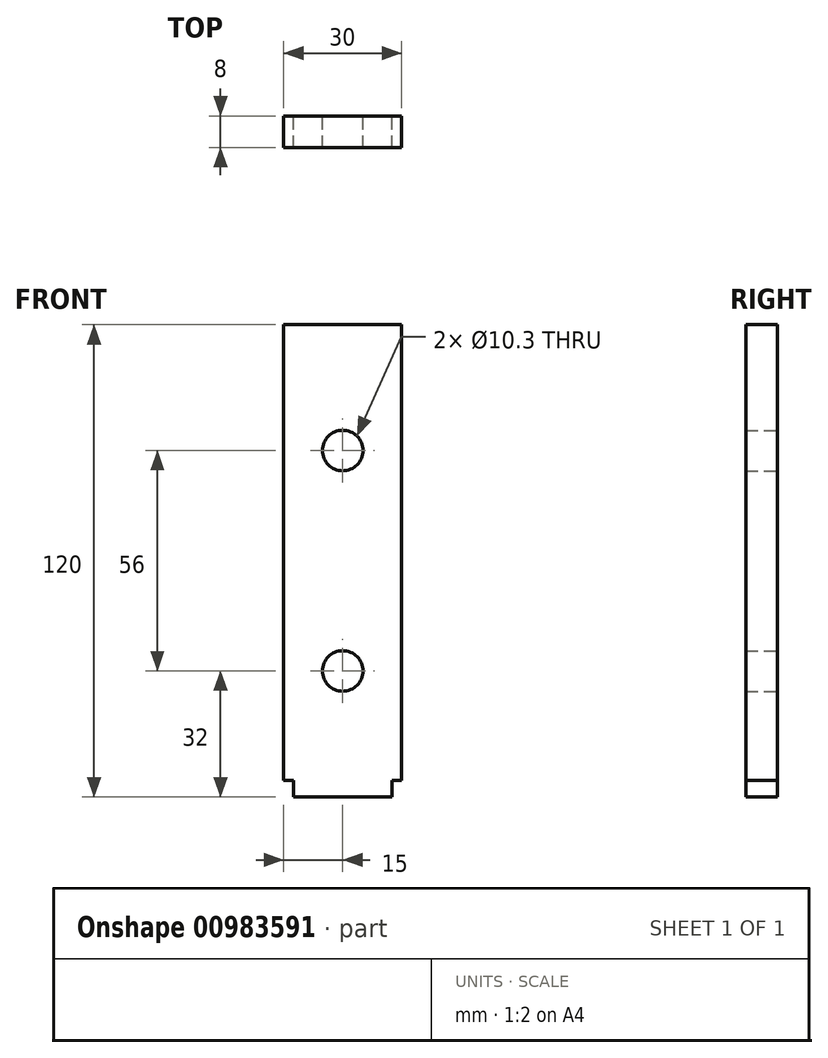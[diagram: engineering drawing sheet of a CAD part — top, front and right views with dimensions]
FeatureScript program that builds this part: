
annotation { "Feature Type Name" : "Feature", "Feature Type Description" : "" }
export const myFeature = defineFeature(function(context is Context, id is Id, definition is map)
    precondition{}
    {
        {
            var Q0;
            Q0=qCreatedBy(makeId("Front.planeOp"),FACE);
            var sketch = newSketch(context, id + "F0", { "sketchPlane" : qUnion([Q0])});
            skLineSegment(sketch, "E0", {"start": v(-15, 0) * mm, "end": v(15, 0) * mm});
            skLineSegment(sketch, "E1", {"start": v(15, 0) * mm, "end": v(15, -115.8) * mm});
            skLineSegment(sketch, "E2", {"start": v(15, -115.8) * mm, "end": v(12.5, -115.8) * mm});
            skLineSegment(sketch, "E3", {"start": v(12.5, -115.8) * mm, "end": v(12.5, -120) * mm});
            skLineSegment(sketch, "E4", {"start": v(12.5, -120) * mm, "end": v(-12.5, -120) * mm});
            skLineSegment(sketch, "E5", {"start": v(-12.5, -120) * mm, "end": v(-12.5, -115.8) * mm});
            skLineSegment(sketch, "E6", {"start": v(-12.5, -115.8) * mm, "end": v(-15, -115.8) * mm});
            skLineSegment(sketch, "E7", {"start": v(-15, -115.8) * mm, "end": v(-15, 0) * mm});
            skLineSegment(sketch, "E8", {"start": v(0, 0) * mm, "end": v(0, -120) * mm, "construction": true});
            skLineSegment(sketch, "E9", {"start": v(-15, -4) * mm, "end": v(15, -4) * mm, "construction": true});
            skCircle(sketch, "E10", {"center": v(0, -32) * mm, "radius": 5.15 * mm});
            skCircle(sketch, "E11", {"center": v(0, -88) * mm, "radius": 5.15 * mm});
            skCircle(sketch, "E12", {"center": v(0, -88) * mm, "radius": 10 * mm, "construction": true});
            skCircle(sketch, "E13", {"center": v(0, -32) * mm, "radius": 10 * mm, "construction": true});
            skSolve(sketch);
        }
        {
            var Q0;
            Q0=makeQuery(id+"F0.imprint","IMPRINT",FACE,{"disambiguationData":[TD([[makeQuery(id+"F0.imprint","IMPRINT",EDGE,{"derivedFrom":sQuery(id+"F0.wireOp",EDGE,"E0")}),-1.0]])]});
            extrude(context, id + "F1", {"entities" : qUnion([Q0]), "depth" : 8 * mm, "offsetDistance" : 25.4 * mm, "symmetric" : true});
        }
    });
